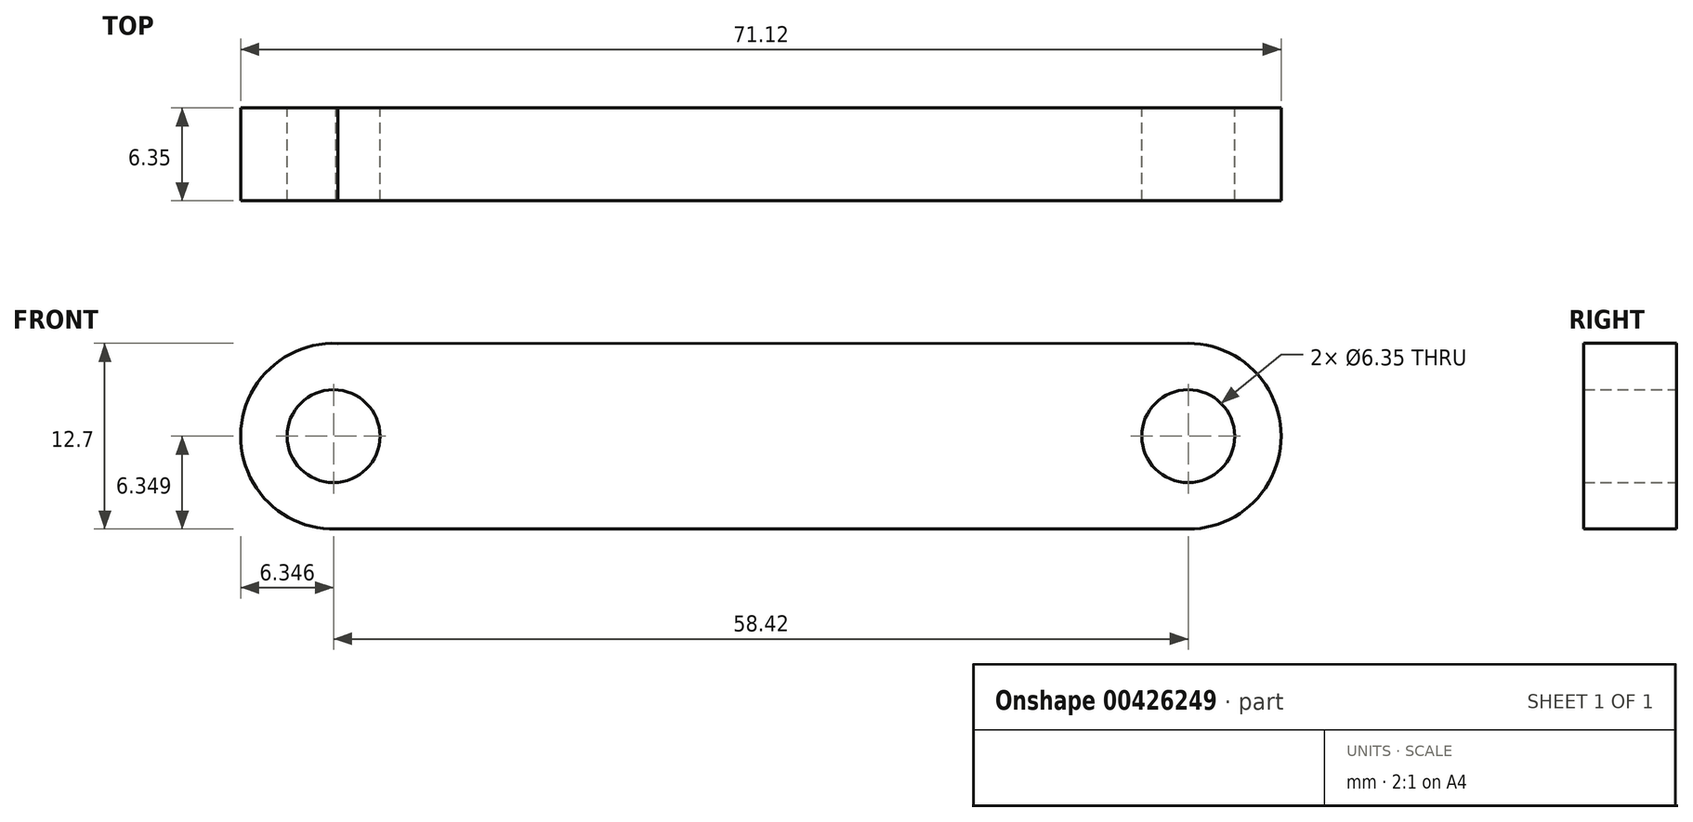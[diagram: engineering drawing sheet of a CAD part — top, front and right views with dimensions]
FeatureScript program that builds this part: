
annotation { "Feature Type Name" : "Feature", "Feature Type Description" : "" }
export const myFeature = defineFeature(function(context is Context, id is Id, definition is map)
    precondition{}
    {
        {
            var Q0;
            Q0=qCreatedBy(makeId("Front.planeOp"),FACE);
            var sketch = newSketch(context, id + "F0", { "sketchPlane" : qUnion([Q0])});
            skCircle(sketch, "E0", {"center": v(-56.1, 0.57) * mm, "radius": 6.35 * mm});
            skCircle(sketch, "E1", {"center": v(-56.1, 0.57) * mm, "radius": 3.18 * mm});
            skCircle(sketch, "E2", {"center": v(2.33, 0.57) * mm, "radius": 6.35 * mm});
            skCircle(sketch, "E3", {"center": v(2.33, 0.57) * mm, "radius": 3.18 * mm});
            skLineSegment(sketch, "E4", {"start": v(-56.4, 6.91) * mm, "end": v(2.33, 6.92) * mm});
            skLineSegment(sketch, "E5", {"start": v(-56.26, -5.78) * mm, "end": v(2.33, -5.78) * mm});
            skSolve(sketch);
        }
        {
            var Q0;
            Q0 = qSketchRegion(id + "F0", true);
            extrude(context, id + "F1", {"entities" : qUnion([Q0]), "depth" : 6.35 * mm});
        }
    });
